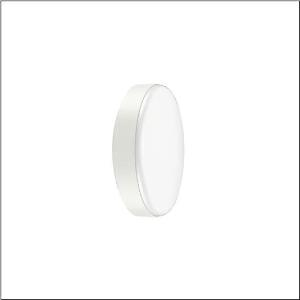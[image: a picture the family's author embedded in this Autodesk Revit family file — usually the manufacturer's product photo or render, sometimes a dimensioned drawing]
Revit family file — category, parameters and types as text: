
# Revit family: round_31_51wc10da32as
name_source: partatom
category: Lighting Fixtures
units: mm (PartAtom-declared; Revit-internal decimal feet)

## family parameters
Cut with Voids When Loaded = No
Host = Face
Light Source = No
Part Type = Normal
Room Calculation Point = No
Round Connector Dimension = Use Diameter
Shared = No

## types (1)
- Round 31 (1 x LED, 2450 lm, 20.4 W, 3000K)
    Apparent Load = 20 VA
    CIE Flux Codes = 44 75 94 94 100
    Color Rendering = 80
    Color Temperature = 3000K
    Default Elevation = 1800 mm
    Description = Round 31, wall and ceiling luminaire, primary optical cover: cover, of PC, opal, light emission: direct distribution, primary light characteristic: symmetric, installation type: surface-mounted, LED, rated luminous flux: 2.450lm, luminous efficacy: 120lm/W, light colour: 830, colour temperature: 3000K, control gear: DALI 2, with terminal, 5-pole, max. 2.5mm², mains connection: 220..240V, AC, 50/60Hz, rated input power: 20.5W, luminaire housing, of PC, traffic white (RAL 9016), diameter: 350mm, brightness and presence sensor, HF sensor, protection rating (complete): IP65, insulation class (complete): insulation class II (safety insulation), certification: CE, impact resistance: IK10, permissible operating ambient temperature: -20..+40°C, permissible storage temperature: -20..+60°C, packaging unit: 1 piece
    Height = 97 mm
    Lamp = 1 x LED
    Lamp Light Flux = 2450 lm
    Lamp Power = 20.4 W
    Lamp count = 1
    Length = 350 mm
    Luminous efficacy = 120 lm/W
    Manufacturer = Siteco
    ModVariant = No
    Model = 51WC10DA32AS
    Mounting Place = Wall
    Mounting Type = Surface mounted
    Number of Poles = 1
    OnlyDefault = Yes
    Power Factor = 1
    Product Name = Round 31
    Product group = wall and ceiling luminaire
    ProductGroupID = 2001
    Protection Class = Protection class II
    Protection Degree = IP 65
    RLX_Detail_Level = 1
    RLX_Emergency_Light_Flux = 0 lm
    RLX_Emergency_Type = 0
    RLX_Emergency_Type_DB = No
    RlxData = <blob elided: 30049 chars, md5=4f397326>
    Socket = socket
    Standby Power = 0 W
    System Light Flux = 2450 lm
    System Power = 20 W
    Type Comments = Product without accessories
    Type Image = l_1007027.jpg
    URL = http://relux.com
    VarID = ---
    Voltage = 0 V
    Weight = 0.00 kg
    Width = 0 mm  [stored 0 ft]

note: [stored X ft] marks values corroborated as IEEE doubles in the binary element streams (Revit-internal decimal feet)

## geometry (parser evidence)
native form markers: Blend x4, Sweep x12
no freeform markers — native parametric forms only
